# Revit family: EKF_EE_ВертикальныйПрофильЩРНМ_PROxima
name_source: partatom
category: Электрооборудование
units: mm (PartAtom-declared; Revit-internal decimal feet)

## family parameters
Всегда вертикально = Нет
На основе рабочей плоскости = Да
Общий = Да
При загрузке вырезать с полостями = Нет
Размер круглого соединителя = Использовать диаметр
Тип детали = Силовой щит
Точка расчета площади = Нет

## types (2) — shared parameters
ADSK_Единица измерения = шт.
ADSK_Завод-изготовитель = EKF
ADSK_Количество = 1
ADSK_Марка = Профиль вертикальный
ADSK_Материал = Сталь_Оцинкованная
ADSK_Обозначение = Профиль вертикальный
ADSK_Размер_Глубина = 40 мм
ADSK_Размер_Ширина = 40 мм
a = 27.2 мм
t = 1.5 мм
Изготовитель = EKF
Отступ = 15 мм
Серия номенклатуры = PROxima
Степень защиты IP = -
ТВ = EKF_2
Тип установки = -
Шаг = 34 мм
zero-valued in all types: ADSK_Масса, Отметка по умолчанию

## per-type parameters (varying)
| type | ADSK_Код изделия | ADSK_Размер_Высота | Тип |
| Профиль вертикальный 1560мм (ЩРНМ-8) | pv-1560 | 1560 мм | 142 мм |
| Профиль вертикальный 1760мм (ЩРНМ-9) | pv-1760 | 1760 мм | 143 мм |

note: column(s) folded — value = type name in every type: ADSK_Наименование
